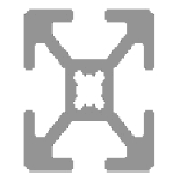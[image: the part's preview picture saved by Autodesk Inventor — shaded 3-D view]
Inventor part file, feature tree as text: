
AUTODESK INVENTOR PART (.ipt)
format: ipt  version: 2013 SP2 (Build 170200200, 200)  size: 236,032 bytes
history: native  units: in
note: dims shown in document units (in); Inventor stores cm internally (conversion verified against a paired STEP export)
features: other x5, sketch x3, plane x1
ambient origin geometry x8: Origin, YZ Plane, XZ Plane, XY Plane, X Axis, Y Axis, Z Axis, Center Point
bodies: Solid1 (feature_tree), Body (feature_tree)
feature tree (9):
  other  "Driven Length"
  other  "Frame Generator"
  other  "Blocks"
  other  "Start Plane"
  other  "End Plane"
  sketch  "Sketch"  dims[d4=0.13in d5=0.0in d6=90.0deg d7=1.9685in]
  sketch  "Sketch2"  dims[d2=0.7874in]
  plane  "Work Plane3"
  sketch  "Sketch3"  dims[d3=2.7559in]
